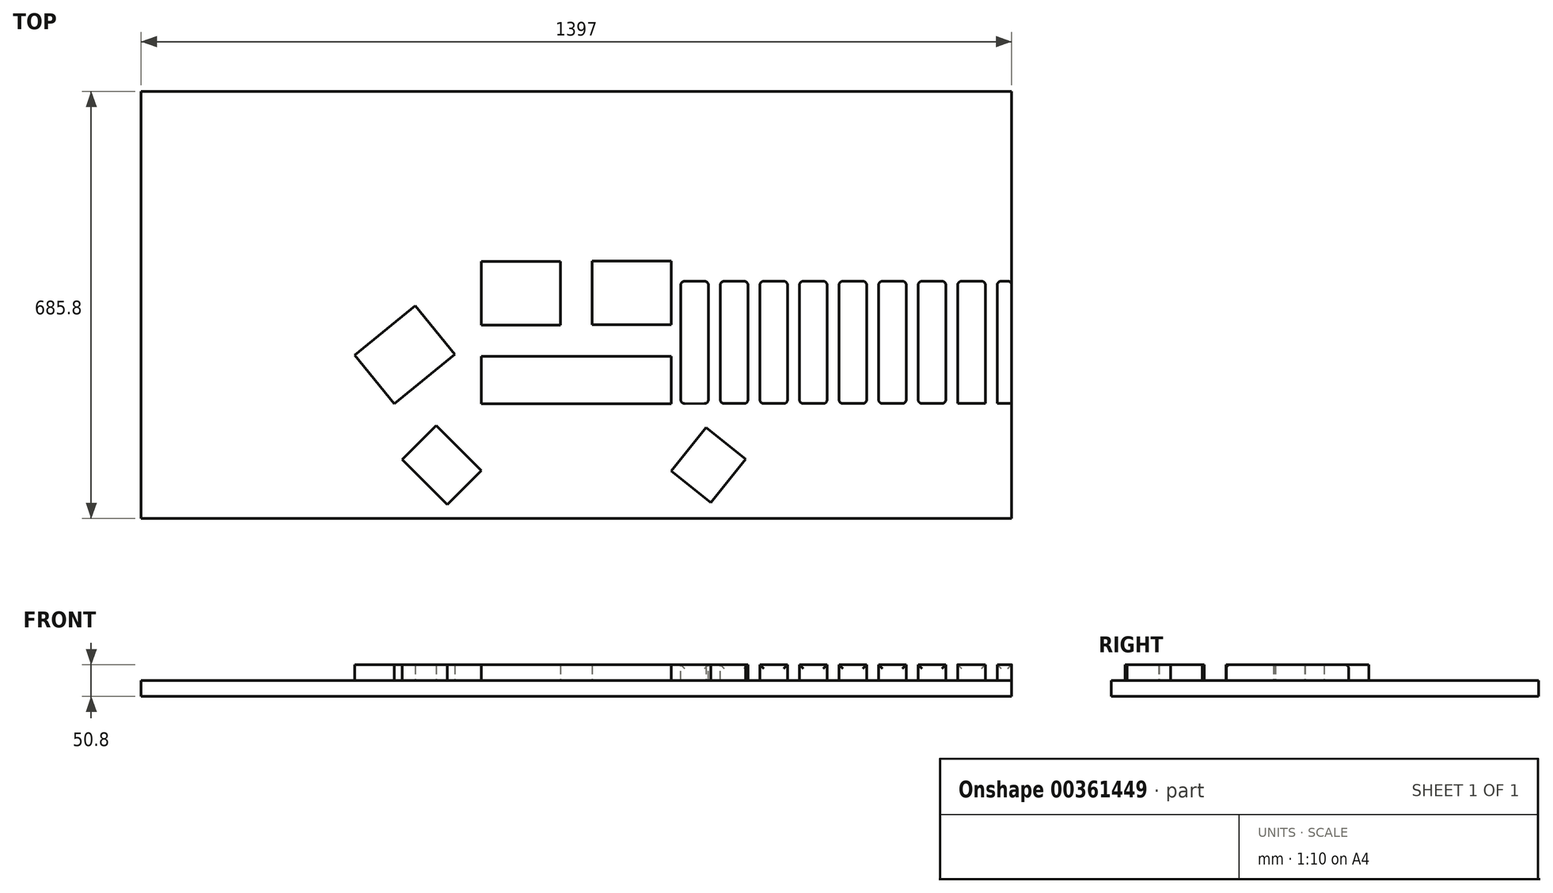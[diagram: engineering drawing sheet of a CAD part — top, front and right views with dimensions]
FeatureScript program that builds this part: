
annotation { "Feature Type Name" : "Feature", "Feature Type Description" : "" }
export const myFeature = defineFeature(function(context is Context, id is Id, definition is map)
    precondition{}
    {
        {
            var Q0;
            Q0=qCreatedBy(makeId("Top.planeOp"),FACE);
            var sketch = newSketch(context, id + "F0", { "sketchPlane" : qUnion([Q0])});
            skLineSegment(sketch, "E0.bottom", {"start": v(698.5, 313.84) * mm, "end": v(-698.5, 313.84) * mm});
            skLineSegment(sketch, "E0.top", {"start": v(698.5, -371.96) * mm, "end": v(-698.5, -371.96) * mm});
            skLineSegment(sketch, "E0.left", {"start": v(698.5, 313.84) * mm, "end": v(698.5, -371.96) * mm});
            skLineSegment(sketch, "E0.right", {"start": v(-698.5, 313.84) * mm, "end": v(-698.5, -371.96) * mm});
            skPoint(sketch, "E0.middle", {"position": v(0, -29.06) * mm});
            skSolve(sketch);
        }
        {
            var Q0;
            Q0=qSketchRegion(id+"F0",true);
            extrude(context, id + "F1", {"entities" : qUnion([Q0]), "depth" : 25.4 * mm});
        }
        {
            var Q0;
            Q0=makeQuery(id+"F1.opExtrude","CAP_FACE",FACE,{"disambiguationData":[OSD([sQuery(id+"F0.wireOp",EDGE,"E0.bottom"),sQuery(id+"F0.wireOp",EDGE,"E0.top"),sQuery(id+"F0.wireOp",EDGE,"E0.left"),sQuery(id+"F0.wireOp",EDGE,"E0.right")])],"isStart":false});
            var sketch = newSketch(context, id + "F2", { "sketchPlane" : qUnion([Q0])});
            skLineSegment(sketch, "E1.bottom", {"start": v(152.4, -111.6) * mm, "end": v(-152.4, -111.6) * mm});
            skLineSegment(sketch, "E1.top", {"start": v(152.4, -187.8) * mm, "end": v(-152.4, -187.8) * mm});
            skLineSegment(sketch, "E1.left", {"start": v(152.4, -111.6) * mm, "end": v(152.4, -187.8) * mm});
            skLineSegment(sketch, "E1.right", {"start": v(-152.4, -111.6) * mm, "end": v(-152.4, -187.8) * mm});
            skPoint(sketch, "E1.middle", {"position": v(0, -149.7) * mm});
            skLineSegment(sketch, "E2.bottom", {"start": v(-194.89, -108.68) * mm, "end": v(-292.1, -187.8) * mm});
            skLineSegment(sketch, "E2.top", {"start": v(-258.39, -30.67) * mm, "end": v(-355.6, -109.8) * mm});
            skLineSegment(sketch, "E2.left", {"start": v(-194.89, -108.68) * mm, "end": v(-258.39, -30.67) * mm});
            skLineSegment(sketch, "E2.right", {"start": v(-292.1, -187.8) * mm, "end": v(-355.6, -109.8) * mm});
            skPoint(sketch, "E2.middle", {"position": v(-275.24, -109.24) * mm});
            skLineSegment(sketch, "E3.bottom", {"start": v(-25.4, -61.33) * mm, "end": v(-152.4, -61.33) * mm});
            skLineSegment(sketch, "E3.top", {"start": v(-25.4, 40.8) * mm, "end": v(-152.4, 40.8) * mm});
            skLineSegment(sketch, "E3.left", {"start": v(-25.4, -61.33) * mm, "end": v(-25.4, 40.8) * mm});
            skLineSegment(sketch, "E3.right", {"start": v(-152.4, -61.33) * mm, "end": v(-152.4, 40.8) * mm});
            skPoint(sketch, "E3.middle", {"position": v(-88.9, -10.27) * mm});
            skPoint(sketch, "E4", {"position": v(-88.9, -61.33) * mm});
            skLineSegment(sketch, "E5.bottom", {"start": v(152.4, -60.8) * mm, "end": v(25.4, -60.8) * mm});
            skLineSegment(sketch, "E5.top", {"start": v(152.4, 41.32) * mm, "end": v(25.4, 41.32) * mm});
            skLineSegment(sketch, "E5.left", {"start": v(152.4, -60.8) * mm, "end": v(152.4, 41.32) * mm});
            skLineSegment(sketch, "E5.right", {"start": v(25.4, -60.8) * mm, "end": v(25.4, 41.32) * mm});
            skPoint(sketch, "E5.middle", {"position": v(88.9, -9.74) * mm});
            skPoint(sketch, "E6", {"position": v(88.9, -60.8) * mm});
            skLineSegment(sketch, "E7.bottom", {"start": v(-152.4, -295.26) * mm, "end": v(-206.87, -349.73) * mm});
            skLineSegment(sketch, "E7.top", {"start": v(-224.93, -222.73) * mm, "end": v(-279.4, -277.2) * mm});
            skLineSegment(sketch, "E7.left", {"start": v(-152.4, -295.26) * mm, "end": v(-224.93, -222.73) * mm});
            skLineSegment(sketch, "E7.right", {"start": v(-206.87, -349.73) * mm, "end": v(-279.4, -277.2) * mm});
            skPoint(sketch, "E7.middle", {"position": v(-215.9, -286.23) * mm});
            skLineSegment(sketch, "E8.bottom", {"start": v(215.9, -346.56) * mm, "end": v(152.4, -295.76) * mm});
            skLineSegment(sketch, "E8.top", {"start": v(271.78, -276.7) * mm, "end": v(208.28, -225.9) * mm});
            skLineSegment(sketch, "E8.left", {"start": v(215.9, -346.56) * mm, "end": v(271.78, -276.7) * mm});
            skLineSegment(sketch, "E8.right", {"start": v(152.4, -295.76) * mm, "end": v(208.28, -225.9) * mm});
            skPoint(sketch, "E8.middle", {"position": v(212.1, -286.23) * mm});
            skSolve(sketch);
        }
        {
            var Q0;
            Q0=qSketchRegion(id+"F2",true);
            extrude(context, id + "F3", {"entities" : qUnion([Q0]), "depth" : 25.4 * mm});
        }
        {
            var Q0;
            Q0=makeQuery(id+"F1.opExtrude","CAP_FACE",FACE,{"disambiguationData":[OSD([sQuery(id+"F0.wireOp",EDGE,"E0.bottom"),sQuery(id+"F0.wireOp",EDGE,"E0.top"),sQuery(id+"F0.wireOp",EDGE,"E0.left"),sQuery(id+"F0.wireOp",EDGE,"E0.right")])],"isStart":false});
            var sketch = newSketch(context, id + "F4", { "sketchPlane" : qUnion([Q0])});
            skLineSegment(sketch, "E9.bottom", {"start": v(802.44, -187.47) * mm, "end": v(167.44, -187.58) * mm});
            skLineSegment(sketch, "E9.top", {"start": v(802.4, 9.1) * mm, "end": v(167.4, 8.99) * mm});
            skLineSegment(sketch, "E9.left", {"start": v(802.44, -187.47) * mm, "end": v(802.4, 9.1) * mm});
            skLineSegment(sketch, "E9.right", {"start": v(167.44, -187.58) * mm, "end": v(167.4, 8.99) * mm});
            skSolve(sketch);
        }
        {
            var Q0;
            Q0=qSketchRegion(id+"F4",true);
            extrude(context, id + "F5", {"entities" : qUnion([Q0]), "operationType" : NewBodyOperationType.ADD, "depth" : 25.4 * mm});
        }
        {
            var Q0;
            Q0=makeQuery(id+"F5.opExtrude","SWEPT_FACE",FACE,{"disambiguationData":[OSD([sQuery(id+"F4.wireOp",EDGE,"E9.bottom")])]});
            var sketch = newSketch(context, id + "F6", { "sketchPlane" : qUnion([Q0])});
            skLineSegment(sketch, "E10.bottom", {"start": v(698.47, 25.4) * mm, "end": v(802.4, 25.4) * mm});
            skLineSegment(sketch, "E10.top", {"start": v(698.47, 50.8) * mm, "end": v(802.4, 50.8) * mm});
            skLineSegment(sketch, "E10.left", {"start": v(698.47, 25.4) * mm, "end": v(698.47, 50.8) * mm});
            skLineSegment(sketch, "E10.right", {"start": v(802.4, 25.4) * mm, "end": v(802.4, 50.8) * mm});
            skPoint(sketch, "E11", {"position": v(167.4, 50.8) * mm});
            skPoint(sketch, "E12", {"position": v(211.86, 50.8) * mm});
            skPoint(sketch, "E13", {"position": v(230.9, 50.8) * mm});
            skPoint(sketch, "E14", {"position": v(275.36, 50.8) * mm});
            skPoint(sketch, "E15", {"position": v(294.4, 50.8) * mm});
            skPoint(sketch, "E16", {"position": v(338.86, 50.8) * mm});
            skPoint(sketch, "E17", {"position": v(357.9, 50.8) * mm});
            skPoint(sketch, "E18", {"position": v(402.36, 50.8) * mm});
            skPoint(sketch, "E19", {"position": v(421.4, 50.8) * mm});
            skPoint(sketch, "E20", {"position": v(465.86, 50.8) * mm});
            skPoint(sketch, "E21", {"position": v(484.9, 50.8) * mm});
            skPoint(sketch, "E22", {"position": v(529.36, 50.8) * mm});
            skPoint(sketch, "E23", {"position": v(548.4, 50.8) * mm});
            skPoint(sketch, "E24", {"position": v(592.86, 50.8) * mm});
            skPoint(sketch, "E25", {"position": v(611.9, 50.8) * mm});
            skPoint(sketch, "E26", {"position": v(656.36, 50.8) * mm});
            skPoint(sketch, "E27", {"position": v(675.4, 50.8) * mm});
            skLineSegment(sketch, "E28.bottom", {"start": v(675.4, 50.8) * mm, "end": v(656.36, 50.8) * mm});
            skLineSegment(sketch, "E28.top", {"start": v(675.4, 25.4) * mm, "end": v(656.36, 25.4) * mm});
            skLineSegment(sketch, "E28.left", {"start": v(675.4, 50.8) * mm, "end": v(675.4, 25.4) * mm});
            skLineSegment(sketch, "E28.right", {"start": v(656.36, 50.8) * mm, "end": v(656.36, 25.4) * mm});
            skLineSegment(sketch, "E29.bottom", {"start": v(611.9, 25.4) * mm, "end": v(592.86, 25.4) * mm});
            skLineSegment(sketch, "E29.top", {"start": v(611.9, 50.8) * mm, "end": v(592.86, 50.8) * mm});
            skLineSegment(sketch, "E29.left", {"start": v(611.9, 25.4) * mm, "end": v(611.9, 50.8) * mm});
            skLineSegment(sketch, "E29.right", {"start": v(592.86, 25.4) * mm, "end": v(592.86, 50.8) * mm});
            skLineSegment(sketch, "E30.bottom", {"start": v(548.4, 25.4) * mm, "end": v(529.36, 25.4) * mm});
            skLineSegment(sketch, "E30.top", {"start": v(548.4, 50.8) * mm, "end": v(529.36, 50.8) * mm});
            skLineSegment(sketch, "E30.left", {"start": v(548.4, 25.4) * mm, "end": v(548.4, 50.8) * mm});
            skLineSegment(sketch, "E30.right", {"start": v(529.36, 25.4) * mm, "end": v(529.36, 50.8) * mm});
            skLineSegment(sketch, "E31.bottom", {"start": v(484.9, 25.4) * mm, "end": v(465.86, 25.4) * mm});
            skLineSegment(sketch, "E31.top", {"start": v(484.9, 50.8) * mm, "end": v(465.86, 50.8) * mm});
            skLineSegment(sketch, "E31.left", {"start": v(484.9, 25.4) * mm, "end": v(484.9, 50.8) * mm});
            skLineSegment(sketch, "E31.right", {"start": v(465.86, 25.4) * mm, "end": v(465.86, 50.8) * mm});
            skLineSegment(sketch, "E32.bottom", {"start": v(421.4, 25.4) * mm, "end": v(402.36, 25.4) * mm});
            skLineSegment(sketch, "E32.top", {"start": v(421.4, 50.8) * mm, "end": v(402.36, 50.8) * mm});
            skLineSegment(sketch, "E32.left", {"start": v(421.4, 25.4) * mm, "end": v(421.4, 50.8) * mm});
            skLineSegment(sketch, "E32.right", {"start": v(402.36, 25.4) * mm, "end": v(402.36, 50.8) * mm});
            skLineSegment(sketch, "E33.bottom", {"start": v(357.9, 25.4) * mm, "end": v(338.86, 25.4) * mm});
            skLineSegment(sketch, "E33.top", {"start": v(357.9, 50.8) * mm, "end": v(338.86, 50.8) * mm});
            skLineSegment(sketch, "E33.left", {"start": v(357.9, 25.4) * mm, "end": v(357.9, 50.8) * mm});
            skLineSegment(sketch, "E33.right", {"start": v(338.86, 25.4) * mm, "end": v(338.86, 50.8) * mm});
            skLineSegment(sketch, "E34.bottom", {"start": v(294.4, 25.4) * mm, "end": v(275.36, 25.4) * mm});
            skLineSegment(sketch, "E34.top", {"start": v(294.4, 50.8) * mm, "end": v(275.36, 50.8) * mm});
            skLineSegment(sketch, "E34.left", {"start": v(294.4, 25.4) * mm, "end": v(294.4, 50.8) * mm});
            skLineSegment(sketch, "E34.right", {"start": v(275.36, 25.4) * mm, "end": v(275.36, 50.8) * mm});
            skLineSegment(sketch, "E35.bottom", {"start": v(230.9, 25.4) * mm, "end": v(211.86, 25.4) * mm});
            skLineSegment(sketch, "E35.top", {"start": v(230.9, 50.8) * mm, "end": v(211.86, 50.8) * mm});
            skLineSegment(sketch, "E35.left", {"start": v(230.9, 25.4) * mm, "end": v(230.9, 50.8) * mm});
            skLineSegment(sketch, "E35.right", {"start": v(211.86, 25.4) * mm, "end": v(211.86, 50.8) * mm});
            skSolve(sketch);
        }
        {
            var Q0;
            Q0=qSketchRegion(id+"F6",true);
            extrude(context, id + "F7", {"entities" : qUnion([Q0]), "operationType" : NewBodyOperationType.REMOVE, "oppositeDirection" : true, "depth" : 203.2 * mm});
        }
        {
            var Q0;
            {var subQ0=sQuery(id+"F4.wireOp",EDGE,"E9.bottom");var subQ1=sQuery(id+"F4.wireOp",EDGE,"E9.right");Q0=makeQuery(id+"F7.boolean.opBoolean","SPLIT",EDGE,{"disambiguationData":[TD([makeQuery(id+"F5.opExtrude","SWEPT_FACE",FACE,{"disambiguationData":[OSD([subQ1])]})])],"derivedFrom":makeQuery(id+"F5.opExtrude","CAP_EDGE",EDGE,{"disambiguationData":[OSD([subQ0])],"isStart":false})});}
            var Q1;
            {var subQ0=sQuery(id+"F4.wireOp",EDGE,"E9.bottom");Q1=makeQuery(id+"F7.boolean.opBoolean","SPLIT",EDGE,{"disambiguationData":[TD([makeQuery(id+"F7.opExtrude","SWEPT_FACE",FACE,{"disambiguationData":[OSD([sQuery(id+"F6.wireOp",EDGE,"E34.right")])]})])],"derivedFrom":makeQuery(id+"F5.opExtrude","CAP_EDGE",EDGE,{"disambiguationData":[OSD([subQ0])],"isStart":false})});}
            var Q2;
            {var subQ0=sQuery(id+"F4.wireOp",EDGE,"E9.bottom");Q2=makeQuery(id+"F7.boolean.opBoolean","SPLIT",EDGE,{"disambiguationData":[TD([makeQuery(id+"F7.opExtrude","SWEPT_FACE",FACE,{"disambiguationData":[OSD([sQuery(id+"F6.wireOp",EDGE,"E33.right")])]})])],"derivedFrom":makeQuery(id+"F5.opExtrude","CAP_EDGE",EDGE,{"disambiguationData":[OSD([subQ0])],"isStart":false})});}
            var Q3;
            {var subQ0=sQuery(id+"F4.wireOp",EDGE,"E9.bottom");Q3=makeQuery(id+"F7.boolean.opBoolean","SPLIT",EDGE,{"disambiguationData":[TD([makeQuery(id+"F7.opExtrude","SWEPT_FACE",FACE,{"disambiguationData":[OSD([sQuery(id+"F6.wireOp",EDGE,"E32.right")])]})])],"derivedFrom":makeQuery(id+"F5.opExtrude","CAP_EDGE",EDGE,{"disambiguationData":[OSD([subQ0])],"isStart":false})});}
            var Q4;
            {var subQ0=sQuery(id+"F4.wireOp",EDGE,"E9.bottom");Q4=makeQuery(id+"F7.boolean.opBoolean","SPLIT",EDGE,{"disambiguationData":[TD([makeQuery(id+"F7.opExtrude","SWEPT_FACE",FACE,{"disambiguationData":[OSD([sQuery(id+"F6.wireOp",EDGE,"E31.right")])]})])],"derivedFrom":makeQuery(id+"F5.opExtrude","CAP_EDGE",EDGE,{"disambiguationData":[OSD([subQ0])],"isStart":false})});}
            var Q5;
            {var subQ0=sQuery(id+"F4.wireOp",EDGE,"E9.bottom");Q5=makeQuery(id+"F7.boolean.opBoolean","SPLIT",EDGE,{"disambiguationData":[TD([makeQuery(id+"F7.opExtrude","SWEPT_FACE",FACE,{"disambiguationData":[OSD([sQuery(id+"F6.wireOp",EDGE,"E30.right")])]})])],"derivedFrom":makeQuery(id+"F5.opExtrude","CAP_EDGE",EDGE,{"disambiguationData":[OSD([subQ0])],"isStart":false})});}
            var Q6;
            {var subQ0=sQuery(id+"F4.wireOp",EDGE,"E9.bottom");Q6=makeQuery(id+"F7.boolean.opBoolean","SPLIT",EDGE,{"disambiguationData":[TD([makeQuery(id+"F7.opExtrude","SWEPT_FACE",FACE,{"disambiguationData":[OSD([sQuery(id+"F6.wireOp",EDGE,"E29.right")])]})])],"derivedFrom":makeQuery(id+"F5.opExtrude","CAP_EDGE",EDGE,{"disambiguationData":[OSD([subQ0])],"isStart":false})});}
            var Q7;
            {var subQ0=sQuery(id+"F4.wireOp",EDGE,"E9.bottom");Q7=makeQuery(id+"F7.boolean.opBoolean","SPLIT",EDGE,{"disambiguationData":[TD([makeQuery(id+"F7.opExtrude","SWEPT_FACE",FACE,{"disambiguationData":[OSD([sQuery(id+"F6.wireOp",EDGE,"E28.right")])]})])],"derivedFrom":makeQuery(id+"F5.opExtrude","CAP_EDGE",EDGE,{"disambiguationData":[OSD([subQ0])],"isStart":false})});}
            var Q8;
            {var subQ0=sQuery(id+"F4.wireOp",EDGE,"E9.top");Q8=makeQuery(id+"F7.boolean.opBoolean","SPLIT",EDGE,{"disambiguationData":[TD([makeQuery(id+"F7.opExtrude","SWEPT_FACE",FACE,{"disambiguationData":[OSD([sQuery(id+"F6.wireOp",EDGE,"E28.right")])]})])],"derivedFrom":makeQuery(id+"F5.opExtrude","CAP_EDGE",EDGE,{"disambiguationData":[OSD([subQ0])],"isStart":false})});}
            var Q9;
            {var subQ0=sQuery(id+"F4.wireOp",EDGE,"E9.top");Q9=makeQuery(id+"F7.boolean.opBoolean","SPLIT",EDGE,{"disambiguationData":[TD([makeQuery(id+"F7.opExtrude","SWEPT_FACE",FACE,{"disambiguationData":[OSD([sQuery(id+"F6.wireOp",EDGE,"E10.left")])]})])],"derivedFrom":makeQuery(id+"F5.opExtrude","CAP_EDGE",EDGE,{"disambiguationData":[OSD([subQ0])],"isStart":false})});}
            var Q10;
            {var subQ0=sQuery(id+"F4.wireOp",EDGE,"E9.bottom");Q10=makeQuery(id+"F7.boolean.opBoolean","SPLIT",EDGE,{"disambiguationData":[TD([makeQuery(id+"F7.opExtrude","SWEPT_FACE",FACE,{"disambiguationData":[OSD([sQuery(id+"F6.wireOp",EDGE,"E10.left")])]})])],"derivedFrom":makeQuery(id+"F5.opExtrude","CAP_EDGE",EDGE,{"disambiguationData":[OSD([subQ0])],"isStart":false})});}
            var Q11;
            {var subQ0=sQuery(id+"F4.wireOp",EDGE,"E9.top");Q11=makeQuery(id+"F7.boolean.opBoolean","SPLIT",EDGE,{"disambiguationData":[TD([makeQuery(id+"F7.opExtrude","SWEPT_FACE",FACE,{"disambiguationData":[OSD([sQuery(id+"F6.wireOp",EDGE,"E29.right")])]})])],"derivedFrom":makeQuery(id+"F5.opExtrude","CAP_EDGE",EDGE,{"disambiguationData":[OSD([subQ0])],"isStart":false})});}
            var Q12;
            {var subQ0=sQuery(id+"F4.wireOp",EDGE,"E9.top");Q12=makeQuery(id+"F7.boolean.opBoolean","SPLIT",EDGE,{"disambiguationData":[TD([makeQuery(id+"F7.opExtrude","SWEPT_FACE",FACE,{"disambiguationData":[OSD([sQuery(id+"F6.wireOp",EDGE,"E30.right")])]})])],"derivedFrom":makeQuery(id+"F5.opExtrude","CAP_EDGE",EDGE,{"disambiguationData":[OSD([subQ0])],"isStart":false})});}
            var Q13;
            {var subQ0=sQuery(id+"F4.wireOp",EDGE,"E9.top");Q13=makeQuery(id+"F7.boolean.opBoolean","SPLIT",EDGE,{"disambiguationData":[TD([makeQuery(id+"F7.opExtrude","SWEPT_FACE",FACE,{"disambiguationData":[OSD([sQuery(id+"F6.wireOp",EDGE,"E31.right")])]})])],"derivedFrom":makeQuery(id+"F5.opExtrude","CAP_EDGE",EDGE,{"disambiguationData":[OSD([subQ0])],"isStart":false})});}
            var Q14;
            {var subQ0=sQuery(id+"F4.wireOp",EDGE,"E9.right");var subQ1=sQuery(id+"F4.wireOp",EDGE,"E9.top");Q14=makeQuery(id+"F7.boolean.opBoolean","SPLIT",EDGE,{"disambiguationData":[TD([makeQuery(id+"F5.opExtrude","SWEPT_FACE",FACE,{"disambiguationData":[OSD([subQ0])]})])],"derivedFrom":makeQuery(id+"F5.opExtrude","CAP_EDGE",EDGE,{"disambiguationData":[OSD([subQ1])],"isStart":false})});}
            var Q15;
            {var subQ0=sQuery(id+"F4.wireOp",EDGE,"E9.top");Q15=makeQuery(id+"F7.boolean.opBoolean","SPLIT",EDGE,{"disambiguationData":[TD([makeQuery(id+"F7.opExtrude","SWEPT_FACE",FACE,{"disambiguationData":[OSD([sQuery(id+"F6.wireOp",EDGE,"E34.right")])]})])],"derivedFrom":makeQuery(id+"F5.opExtrude","CAP_EDGE",EDGE,{"disambiguationData":[OSD([subQ0])],"isStart":false})});}
            var Q16;
            {var subQ0=sQuery(id+"F4.wireOp",EDGE,"E9.top");Q16=makeQuery(id+"F7.boolean.opBoolean","SPLIT",EDGE,{"disambiguationData":[TD([makeQuery(id+"F7.opExtrude","SWEPT_FACE",FACE,{"disambiguationData":[OSD([sQuery(id+"F6.wireOp",EDGE,"E33.right")])]})])],"derivedFrom":makeQuery(id+"F5.opExtrude","CAP_EDGE",EDGE,{"disambiguationData":[OSD([subQ0])],"isStart":false})});}
            var Q17;
            {var subQ0=sQuery(id+"F4.wireOp",EDGE,"E9.top");Q17=makeQuery(id+"F7.boolean.opBoolean","SPLIT",EDGE,{"disambiguationData":[TD([makeQuery(id+"F7.opExtrude","SWEPT_FACE",FACE,{"disambiguationData":[OSD([sQuery(id+"F6.wireOp",EDGE,"E32.right")])]})])],"derivedFrom":makeQuery(id+"F5.opExtrude","CAP_EDGE",EDGE,{"disambiguationData":[OSD([subQ0])],"isStart":false})});}
            var Q18;
            Q18=makeQuery(id+"F5.opExtrude","SWEPT_EDGE",EDGE,{"disambiguationData":[OSD([sQuery(id+"F4.wireOp",EDGE,"E9.bottom"),sQuery(id+"F4.wireOp",EDGE,"E9.right")])]});
            var Q19;
            Q19=makeQuery(id+"F7.boolean.opBoolean","COPY",EDGE,{"derivedFrom":makeQuery(id+"F7.opExtrude","CAP_EDGE",EDGE,{"disambiguationData":[OSD([sQuery(id+"F6.wireOp",EDGE,"E35.right")])],"isStart":true})});
            var Q20;
            Q20=makeQuery(id+"F7.boolean.opBoolean","COPY",EDGE,{"derivedFrom":makeQuery(id+"F7.opExtrude","CAP_EDGE",EDGE,{"disambiguationData":[OSD([sQuery(id+"F6.wireOp",EDGE,"E35.left")])],"isStart":true})});
            var Q21;
            Q21=makeQuery(id+"F7.boolean.opBoolean","COPY",EDGE,{"derivedFrom":makeQuery(id+"F7.opExtrude","CAP_EDGE",EDGE,{"disambiguationData":[OSD([sQuery(id+"F6.wireOp",EDGE,"E34.right")])],"isStart":true})});
            var Q22;
            Q22=makeQuery(id+"F7.boolean.opBoolean","COPY",EDGE,{"derivedFrom":makeQuery(id+"F7.opExtrude","CAP_EDGE",EDGE,{"disambiguationData":[OSD([sQuery(id+"F6.wireOp",EDGE,"E34.left")])],"isStart":true})});
            var Q23;
            Q23=makeQuery(id+"F7.boolean.opBoolean","COPY",EDGE,{"derivedFrom":makeQuery(id+"F7.opExtrude","CAP_EDGE",EDGE,{"disambiguationData":[OSD([sQuery(id+"F6.wireOp",EDGE,"E33.right")])],"isStart":true})});
            var Q24;
            Q24=makeQuery(id+"F7.boolean.opBoolean","COPY",EDGE,{"derivedFrom":makeQuery(id+"F7.opExtrude","CAP_EDGE",EDGE,{"disambiguationData":[OSD([sQuery(id+"F6.wireOp",EDGE,"E33.left")])],"isStart":true})});
            var Q25;
            Q25=makeQuery(id+"F7.boolean.opBoolean","COPY",EDGE,{"derivedFrom":makeQuery(id+"F7.opExtrude","CAP_EDGE",EDGE,{"disambiguationData":[OSD([sQuery(id+"F6.wireOp",EDGE,"E32.right")])],"isStart":true})});
            var Q26;
            Q26=makeQuery(id+"F7.boolean.opBoolean","COPY",EDGE,{"derivedFrom":makeQuery(id+"F7.opExtrude","CAP_EDGE",EDGE,{"disambiguationData":[OSD([sQuery(id+"F6.wireOp",EDGE,"E32.left")])],"isStart":true})});
            var Q27;
            Q27=makeQuery(id+"F7.boolean.opBoolean","COPY",EDGE,{"derivedFrom":makeQuery(id+"F7.opExtrude","CAP_EDGE",EDGE,{"disambiguationData":[OSD([sQuery(id+"F6.wireOp",EDGE,"E31.right")])],"isStart":true})});
            var Q28;
            Q28=makeQuery(id+"F7.boolean.opBoolean","COPY",EDGE,{"derivedFrom":makeQuery(id+"F7.opExtrude","CAP_EDGE",EDGE,{"disambiguationData":[OSD([sQuery(id+"F6.wireOp",EDGE,"E31.left")])],"isStart":true})});
            var Q29;
            Q29=makeQuery(id+"F7.boolean.opBoolean","COPY",EDGE,{"derivedFrom":makeQuery(id+"F7.opExtrude","CAP_EDGE",EDGE,{"disambiguationData":[OSD([sQuery(id+"F6.wireOp",EDGE,"E30.right")])],"isStart":true})});
            var Q30;
            Q30=makeQuery(id+"F7.boolean.opBoolean","COPY",EDGE,{"derivedFrom":makeQuery(id+"F7.opExtrude","CAP_EDGE",EDGE,{"disambiguationData":[OSD([sQuery(id+"F6.wireOp",EDGE,"E30.left")])],"isStart":true})});
            var Q31;
            Q31=makeQuery(id+"F7.boolean.opBoolean","COPY",EDGE,{"derivedFrom":makeQuery(id+"F7.opExtrude","CAP_EDGE",EDGE,{"disambiguationData":[OSD([sQuery(id+"F6.wireOp",EDGE,"E29.right")])],"isStart":true})});
            var Q32;
            Q32=makeQuery(id+"F7.boolean.opBoolean","COPY",EDGE,{"derivedFrom":makeQuery(id+"F7.opExtrude","CAP_EDGE",EDGE,{"disambiguationData":[OSD([sQuery(id+"F6.wireOp",EDGE,"E29.left")])],"isStart":true})});
            var Q33;
            Q33=makeQuery(id+"F7.boolean.opBoolean","COPY",EDGE,{"derivedFrom":makeQuery(id+"F7.opExtrude","CAP_EDGE",EDGE,{"disambiguationData":[OSD([sQuery(id+"F6.wireOp",EDGE,"E28.right")])],"isStart":true})});
            var Q34;
            Q34=makeQuery(id+"F7.boolean.opBoolean","INTERSECT",EDGE,{"derivedFrom":[makeQuery(id+"F5.opExtrude","SWEPT_FACE",FACE,{"disambiguationData":[OSD([sQuery(id+"F4.wireOp",EDGE,"E9.top")])]}),makeQuery(id+"F7.opExtrude","SWEPT_FACE",FACE,{"disambiguationData":[OSD([sQuery(id+"F6.wireOp",EDGE,"E35.right")])]})]});
            var Q35;
            Q35=makeQuery(id+"F5.opExtrude","SWEPT_EDGE",EDGE,{"disambiguationData":[OSD([sQuery(id+"F4.wireOp",EDGE,"E9.top"),sQuery(id+"F4.wireOp",EDGE,"E9.right")])]});
            var Q36;
            Q36=makeQuery(id+"F7.boolean.opBoolean","INTERSECT",EDGE,{"derivedFrom":[makeQuery(id+"F5.opExtrude","SWEPT_FACE",FACE,{"disambiguationData":[OSD([sQuery(id+"F4.wireOp",EDGE,"E9.top")])]}),makeQuery(id+"F7.opExtrude","SWEPT_FACE",FACE,{"disambiguationData":[OSD([sQuery(id+"F6.wireOp",EDGE,"E35.left")])]})]});
            var Q37;
            Q37=makeQuery(id+"F7.boolean.opBoolean","INTERSECT",EDGE,{"derivedFrom":[makeQuery(id+"F5.opExtrude","SWEPT_FACE",FACE,{"disambiguationData":[OSD([sQuery(id+"F4.wireOp",EDGE,"E9.top")])]}),makeQuery(id+"F7.opExtrude","SWEPT_FACE",FACE,{"disambiguationData":[OSD([sQuery(id+"F6.wireOp",EDGE,"E34.right")])]})]});
            var Q38;
            Q38=makeQuery(id+"F7.boolean.opBoolean","INTERSECT",EDGE,{"derivedFrom":[makeQuery(id+"F5.opExtrude","SWEPT_FACE",FACE,{"disambiguationData":[OSD([sQuery(id+"F4.wireOp",EDGE,"E9.top")])]}),makeQuery(id+"F7.opExtrude","SWEPT_FACE",FACE,{"disambiguationData":[OSD([sQuery(id+"F6.wireOp",EDGE,"E34.left")])]})]});
            var Q39;
            Q39=makeQuery(id+"F7.boolean.opBoolean","INTERSECT",EDGE,{"derivedFrom":[makeQuery(id+"F5.opExtrude","SWEPT_FACE",FACE,{"disambiguationData":[OSD([sQuery(id+"F4.wireOp",EDGE,"E9.top")])]}),makeQuery(id+"F7.opExtrude","SWEPT_FACE",FACE,{"disambiguationData":[OSD([sQuery(id+"F6.wireOp",EDGE,"E33.right")])]})]});
            var Q40;
            Q40=makeQuery(id+"F7.boolean.opBoolean","INTERSECT",EDGE,{"derivedFrom":[makeQuery(id+"F5.opExtrude","SWEPT_FACE",FACE,{"disambiguationData":[OSD([sQuery(id+"F4.wireOp",EDGE,"E9.top")])]}),makeQuery(id+"F7.opExtrude","SWEPT_FACE",FACE,{"disambiguationData":[OSD([sQuery(id+"F6.wireOp",EDGE,"E33.left")])]})]});
            var Q41;
            Q41=makeQuery(id+"F7.boolean.opBoolean","INTERSECT",EDGE,{"derivedFrom":[makeQuery(id+"F5.opExtrude","SWEPT_FACE",FACE,{"disambiguationData":[OSD([sQuery(id+"F4.wireOp",EDGE,"E9.top")])]}),makeQuery(id+"F7.opExtrude","SWEPT_FACE",FACE,{"disambiguationData":[OSD([sQuery(id+"F6.wireOp",EDGE,"E32.right")])]})]});
            var Q42;
            Q42=makeQuery(id+"F7.boolean.opBoolean","INTERSECT",EDGE,{"derivedFrom":[makeQuery(id+"F5.opExtrude","SWEPT_FACE",FACE,{"disambiguationData":[OSD([sQuery(id+"F4.wireOp",EDGE,"E9.top")])]}),makeQuery(id+"F7.opExtrude","SWEPT_FACE",FACE,{"disambiguationData":[OSD([sQuery(id+"F6.wireOp",EDGE,"E32.left")])]})]});
            var Q43;
            Q43=makeQuery(id+"F7.boolean.opBoolean","INTERSECT",EDGE,{"derivedFrom":[makeQuery(id+"F5.opExtrude","SWEPT_FACE",FACE,{"disambiguationData":[OSD([sQuery(id+"F4.wireOp",EDGE,"E9.top")])]}),makeQuery(id+"F7.opExtrude","SWEPT_FACE",FACE,{"disambiguationData":[OSD([sQuery(id+"F6.wireOp",EDGE,"E31.right")])]})]});
            var Q44;
            Q44=makeQuery(id+"F7.boolean.opBoolean","INTERSECT",EDGE,{"derivedFrom":[makeQuery(id+"F5.opExtrude","SWEPT_FACE",FACE,{"disambiguationData":[OSD([sQuery(id+"F4.wireOp",EDGE,"E9.top")])]}),makeQuery(id+"F7.opExtrude","SWEPT_FACE",FACE,{"disambiguationData":[OSD([sQuery(id+"F6.wireOp",EDGE,"E31.left")])]})]});
            var Q45;
            Q45=makeQuery(id+"F7.boolean.opBoolean","INTERSECT",EDGE,{"derivedFrom":[makeQuery(id+"F5.opExtrude","SWEPT_FACE",FACE,{"disambiguationData":[OSD([sQuery(id+"F4.wireOp",EDGE,"E9.top")])]}),makeQuery(id+"F7.opExtrude","SWEPT_FACE",FACE,{"disambiguationData":[OSD([sQuery(id+"F6.wireOp",EDGE,"E30.right")])]})]});
            var Q46;
            Q46=makeQuery(id+"F7.boolean.opBoolean","INTERSECT",EDGE,{"derivedFrom":[makeQuery(id+"F5.opExtrude","SWEPT_FACE",FACE,{"disambiguationData":[OSD([sQuery(id+"F4.wireOp",EDGE,"E9.top")])]}),makeQuery(id+"F7.opExtrude","SWEPT_FACE",FACE,{"disambiguationData":[OSD([sQuery(id+"F6.wireOp",EDGE,"E30.left")])]})]});
            var Q47;
            Q47=makeQuery(id+"F7.boolean.opBoolean","INTERSECT",EDGE,{"derivedFrom":[makeQuery(id+"F5.opExtrude","SWEPT_FACE",FACE,{"disambiguationData":[OSD([sQuery(id+"F4.wireOp",EDGE,"E9.top")])]}),makeQuery(id+"F7.opExtrude","SWEPT_FACE",FACE,{"disambiguationData":[OSD([sQuery(id+"F6.wireOp",EDGE,"E29.right")])]})]});
            var Q48;
            Q48=makeQuery(id+"F7.boolean.opBoolean","INTERSECT",EDGE,{"derivedFrom":[makeQuery(id+"F5.opExtrude","SWEPT_FACE",FACE,{"disambiguationData":[OSD([sQuery(id+"F4.wireOp",EDGE,"E9.top")])]}),makeQuery(id+"F7.opExtrude","SWEPT_FACE",FACE,{"disambiguationData":[OSD([sQuery(id+"F6.wireOp",EDGE,"E29.left")])]})]});
            var Q49;
            Q49=makeQuery(id+"F7.boolean.opBoolean","INTERSECT",EDGE,{"derivedFrom":[makeQuery(id+"F5.opExtrude","SWEPT_FACE",FACE,{"disambiguationData":[OSD([sQuery(id+"F4.wireOp",EDGE,"E9.top")])]}),makeQuery(id+"F7.opExtrude","SWEPT_FACE",FACE,{"disambiguationData":[OSD([sQuery(id+"F6.wireOp",EDGE,"E28.right")])]})]});
            var Q50;
            Q50=makeQuery(id+"F7.boolean.opBoolean","INTERSECT",EDGE,{"derivedFrom":[makeQuery(id+"F5.opExtrude","SWEPT_FACE",FACE,{"disambiguationData":[OSD([sQuery(id+"F4.wireOp",EDGE,"E9.top")])]}),makeQuery(id+"F7.opExtrude","SWEPT_FACE",FACE,{"disambiguationData":[OSD([sQuery(id+"F6.wireOp",EDGE,"E28.left")])]})]});
            var Q51;
            Q51=makeQuery(id+"F7.boolean.opBoolean","INTERSECT",EDGE,{"derivedFrom":[makeQuery(id+"F5.opExtrude","SWEPT_FACE",FACE,{"disambiguationData":[OSD([sQuery(id+"F4.wireOp",EDGE,"E9.top")])]}),makeQuery(id+"F7.opExtrude","SWEPT_FACE",FACE,{"disambiguationData":[OSD([sQuery(id+"F6.wireOp",EDGE,"E10.left")])]})]});
            fillet(context, id + "F8", {"entities" : qUnion([Q0, Q1, Q2, Q3, Q4, Q5, Q6, Q7, Q8, Q9, Q10, Q11, Q12, Q13, Q14, Q15, Q16, Q17, Q18, Q19, Q20, Q21, Q22, Q23, Q24, Q25, Q26, Q27, Q28, Q29, Q30, Q31, Q32, Q33, Q34, Q35, Q36, Q37, Q38, Q39, Q40, Q41, Q42, Q43, Q44, Q45, Q46, Q47, Q48, Q49, Q50, Q51]), "radius" : 6.35 * mm, "tangentPropagation" : true, "allowEdgeOverflow" : false});
        }
    });
